# Revit family: DC_Holyoake_OutsideLouver_OHL-C-34_supply_13
name_source: partatom
category: Air Terminals
revit_build: Autodesk Revit 2014 (Build: 20130308_1515(x64)
units: mm (PartAtom-declared; Revit-internal decimal feet)

## types (1)
- OHL-C-34
    Accessories = Aluminium Bird mesh or insect mesh (fibreglass)
    Blade Array Count = 10.105263
    Blade Count = 9
    Blade Cut Setout = 342 mm
    Blade Height = 56.77 mm  [stored 0.186253 ft]
    Blade Length = 454 mm  [stored 1.4895 ft]
    Blade Offset = 3 mm  [stored 0.00984252 ft]
    Blade Pitch = 38 mm
    Blade Setout = 384 mm
    Channel Thickness = 40.14 mm  [stored 0.131693 ft]
    Channel Width = 25.4 mm  [stored 0.0833333 ft]
    Description = Weather Louvres shall be Holyoake Model OHL-C-34 curved profile 34mm louvred blades set at 38mm centres and constructed in a channel (C) frame to suit the installation profile.  Weather Louvres shall be of extruded aluminium construction and finished in natural anodised or powdercoat and fitted with accessories and dampers where indicated as manufactured by Holyoake.
    Exact Neck Height = 390 mm  [stored 1.27953 ft]
    Exact Neck Width = 460 mm  [stored 1.50919 ft]
    Exact Overall Channel Height = 438.2 mm
    Exact Overall Channel Width = 508.2 mm
    Holyoake Product Range = Outside Louvres
    Manufacturer = Holyoake
    Material - Body = Holyoake Aluminium
    Material - Face = Holyoake Aluminium
    Max Flow = 2000.0 L/s
    Min Flow = 100.0 L/s
    Model = OHL-C-34
    Noise Level NC Max = 0.00 NC
    Noise Level NC Min = 0.00 NC
    Nominal Height = 396 mm  [stored 1.29921 ft]
    Nominal Width = 466 mm  [stored 1.52887 ft]
    Overall Opening Height = 366 mm
    Overall Opening Width = 436 mm
    Static Pressure Max = 60.0 Pa
    Static Pressure Min = 10.0 Pa
    Top Blade Height = 42 mm
    Type Comments = 34mm Horizontal Curved Profile Louvers in Channel Surround
    URL = http://www.holyoake.com

note: [stored X ft] marks values corroborated as IEEE doubles in the binary element streams (Revit-internal decimal feet)

## geometry (parser evidence)
native form markers: Blend x6, Sweep x5
no freeform markers — native parametric forms only
